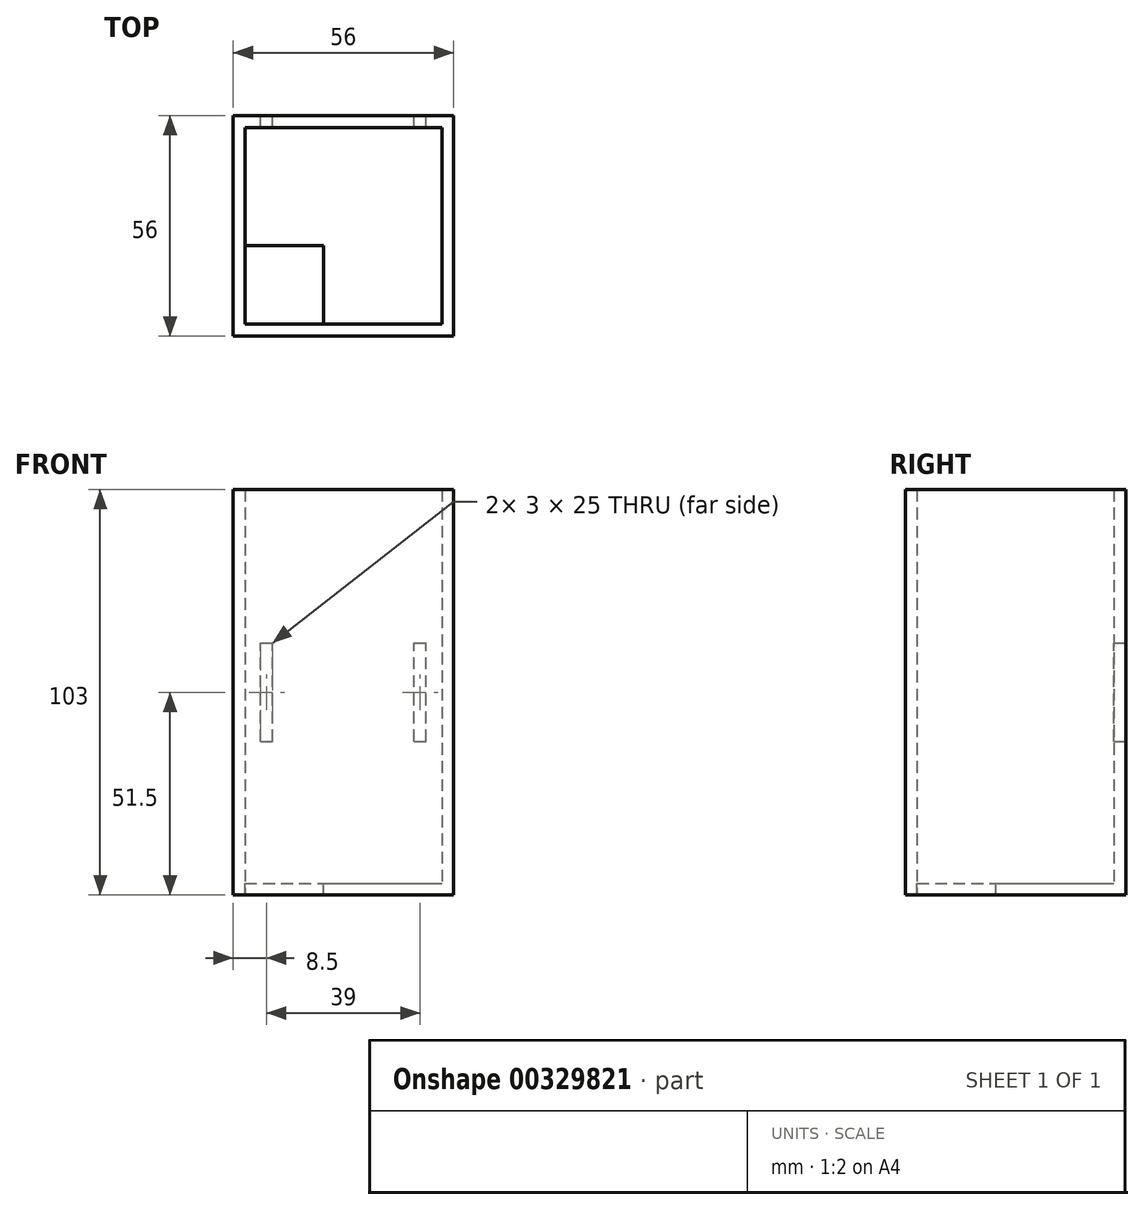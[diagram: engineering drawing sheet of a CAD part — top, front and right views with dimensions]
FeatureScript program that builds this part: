
annotation { "Feature Type Name" : "Feature", "Feature Type Description" : "" }
export const myFeature = defineFeature(function(context is Context, id is Id, definition is map)
    precondition{}
    {
        {
            assignVariable(context, id + "F0", {"name" : "WallTh", "anyValue" : 3});
        }
        {
            assignVariable(context, id + "F1", {"name" : "Height", "anyValue" : 100});
        }
        {
            var Q0;
            Q0=qCreatedBy(makeId("Top.planeOp"),FACE);
            var sketch = newSketch(context, id + "F2", { "sketchPlane" : qUnion([Q0])});
            skLineSegment(sketch, "E0.bottom", {"start": v(0, 0) * mm, "end": v(56, 0) * mm});
            skLineSegment(sketch, "E0.top", {"start": v(0, 56) * mm, "end": v(56, 56) * mm});
            skLineSegment(sketch, "E0.left", {"start": v(0, 0) * mm, "end": v(0, 56) * mm});
            skLineSegment(sketch, "E0.right", {"start": v(56, 0) * mm, "end": v(56, 56) * mm});
            skLineSegment(sketch, "E1.bottom", {"start": v(3, 3) * mm, "end": v(53, 3) * mm});
            skLineSegment(sketch, "E1.top", {"start": v(3, 53) * mm, "end": v(53, 53) * mm});
            skLineSegment(sketch, "E1.left", {"start": v(3, 3) * mm, "end": v(3, 53) * mm});
            skLineSegment(sketch, "E1.right", {"start": v(53, 3) * mm, "end": v(53, 53) * mm});
            skLineSegment(sketch, "E2", {"start": v(28, 53) * mm, "end": v(28, 56) * mm, "construction": true});
            skLineSegment(sketch, "E3", {"start": v(53, 28) * mm, "end": v(56, 28) * mm, "construction": true});
            skSolve(sketch);
        }
        {
            var Q0;
            Q0 = qSketchRegion(id + "F2", true);
            extrude(context, id + "F3", {"entities" : qUnion([Q0]), "depth" : (getVariable(context, 'Height')) * mm});
        }
        {
            var Q0;
            Q0=makeQuery(id+"F2.imprint","IMPRINT",FACE,{"disambiguationData":[TD([[makeQuery(id+"F2.imprint","IMPRINT",EDGE,{"derivedFrom":sQuery(id+"F2.wireOp",EDGE,"E0.bottom")}),1.0]])]});
            var Q1;
            Q1=makeQuery(id+"F2.imprint","IMPRINT",FACE,{"disambiguationData":[TD([[makeQuery(id+"F2.imprint","IMPRINT",EDGE,{"derivedFrom":sQuery(id+"F2.wireOp",EDGE,"E1.bottom")}),1.0]])]});
            extrude(context, id + "F4", {"entities" : qUnion([Q0, Q1]), "operationType" : NewBodyOperationType.ADD, "oppositeDirection" : true, "depth" : (getVariable(context, 'WallTh')) * mm});
        }
        {
            var Q0;
            Q0=makeQuery(id+"F4.opExtrude","CAP_FACE",FACE,{"disambiguationData":[OSD([sQuery(id+"F2.wireOp",EDGE,"E0.bottom"),sQuery(id+"F2.wireOp",EDGE,"E0.top"),sQuery(id+"F2.wireOp",EDGE,"E0.left"),sQuery(id+"F2.wireOp",EDGE,"E0.right")])],"isStart":true});
            var sketch = newSketch(context, id + "F5", { "sketchPlane" : qUnion([Q0])});
            skLineSegment(sketch, "E4.bottom", {"start": v(3, 3) * mm, "end": v(23, 3) * mm});
            skLineSegment(sketch, "E4.top", {"start": v(3, 23) * mm, "end": v(23, 23) * mm});
            skLineSegment(sketch, "E4.left", {"start": v(3, 3) * mm, "end": v(3, 23) * mm});
            skLineSegment(sketch, "E4.right", {"start": v(23, 3) * mm, "end": v(23, 23) * mm});
            skSolve(sketch);
        }
        {
            var Q0;
            Q0 = qSketchRegion(id + "F5", true);
            extrude(context, id + "F6", {"entities" : qUnion([Q0]), "operationType" : NewBodyOperationType.REMOVE, "endBound" : BoundingType.UP_TO_NEXT, "oppositeDirection" : true, "depth" : 25 * mm});
        }
        {
            var Q0;
            {var subQ0=sQuery(id+"F2.wireOp",EDGE,"E0.top");Q0=makeQuery(id+"F4.boolean.opBoolean","MERGE",FACE,{"derivedFrom":[makeQuery(id+"F3.opExtrude","SWEPT_FACE",FACE,{"disambiguationData":[OSD([subQ0])]}),makeQuery(id+"F4.opExtrude","SWEPT_FACE",FACE,{"disambiguationData":[OSD([subQ0])]})]});}
            var sketch = newSketch(context, id + "F7", { "sketchPlane" : qUnion([Q0])});
            skLineSegment(sketch, "E5.bottom", {"start": v(-49, 61) * mm, "end": v(-46, 61) * mm});
            skLineSegment(sketch, "E5.top", {"start": v(-49, 36) * mm, "end": v(-46, 36) * mm});
            skLineSegment(sketch, "E5.left", {"start": v(-49, 61) * mm, "end": v(-49, 36) * mm});
            skLineSegment(sketch, "E5.right", {"start": v(-46, 61) * mm, "end": v(-46, 36) * mm});
            skLineSegment(sketch, "E6.bottom", {"start": v(-10, 61) * mm, "end": v(-7, 61) * mm});
            skLineSegment(sketch, "E6.top", {"start": v(-10, 36) * mm, "end": v(-7, 36) * mm});
            skLineSegment(sketch, "E6.left", {"start": v(-10, 61) * mm, "end": v(-10, 36) * mm});
            skLineSegment(sketch, "E6.right", {"start": v(-7, 61) * mm, "end": v(-7, 36) * mm});
            skLineSegment(sketch, "E7", {"start": v(-49, 61) * mm, "end": v(-49, 100) * mm, "construction": true});
            skLineSegment(sketch, "E8", {"start": v(-49, 36) * mm, "end": v(-49, -3) * mm, "construction": true});
            skLineSegment(sketch, "E9", {"start": v(-49, 48.5) * mm, "end": v(-56, 48.5) * mm, "construction": true});
            skLineSegment(sketch, "E10", {"start": v(-7, 48.5) * mm, "end": v(0, 48.5) * mm, "construction": true});
            skSolve(sketch);
        }
        {
            var Q0;
            Q0 = qSketchRegion(id + "F7", true);
            extrude(context, id + "F8", {"entities" : qUnion([Q0]), "operationType" : NewBodyOperationType.REMOVE, "endBound" : BoundingType.UP_TO_NEXT, "oppositeDirection" : true, "depth" : 25 * mm});
        }
    });
